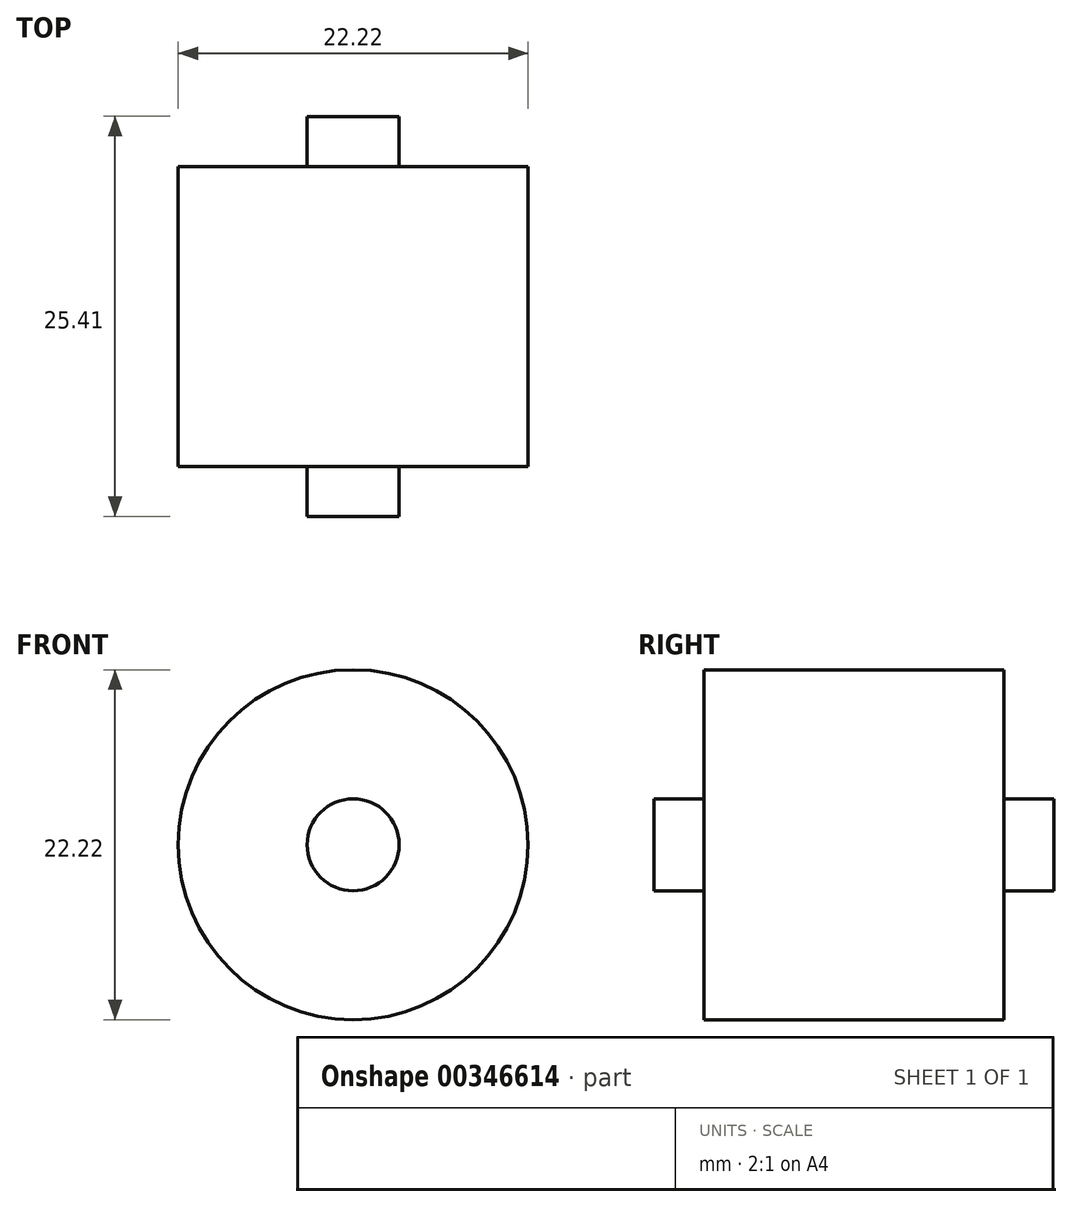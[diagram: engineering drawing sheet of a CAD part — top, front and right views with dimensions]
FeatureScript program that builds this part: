
annotation { "Feature Type Name" : "Feature", "Feature Type Description" : "" }
export const myFeature = defineFeature(function(context is Context, id is Id, definition is map)
    precondition{}
    {
        {
            var Q0;
            Q0=qCreatedBy(makeId("Front.planeOp"),FACE);
            var sketch = newSketch(context, id + "F0", { "sketchPlane" : qUnion([Q0])});
            skCircle(sketch, "E0", {"center": v(0, 0) * mm, "radius": 11.11 * mm});
            skSolve(sketch);
        }
        {
            var Q0;
            Q0 = qSketchRegion(id + "F0", true);
            extrude(context, id + "F1", {"entities" : qUnion([Q0]), "depth" : 19.05 * mm});
        }
        {
            var Q0;
            Q0=makeQuery(id+"F1.opExtrude","CAP_FACE",FACE,{"disambiguationData":[OSD([sQuery(id+"F0.wireOp",EDGE,"E0")])],"isStart":false});
            var sketch = newSketch(context, id + "F2", { "sketchPlane" : qUnion([Q0])});
            skCircle(sketch, "E1.0", {"center": v(0, 0) * mm, "radius": 11.11 * mm});
            skCircle(sketch, "E2", {"center": v(0, 0) * mm, "radius": 2.92 * mm});
            skSolve(sketch);
        }
        {
            var Q0;
            Q0=makeQuery(id+"F2.imprint","IMPRINT",FACE,{"disambiguationData":[TD([[makeQuery(id+"F2.imprint","IMPRINT",EDGE,{"derivedFrom":sQuery(id+"F2.wireOp",EDGE,"E2")}),1.0]])]});
            var Q1;
            Q1=sQuery(id+"F2.wireOp",EDGE,"E2");
            extrude(context, id + "F3", {"entities" : qUnion([Q0]), "operationType" : NewBodyOperationType.ADD, "surfaceEntities" : qUnion([Q1]), "depth" : 3.17 * mm});
        }
        {
            var Q0;
            Q0=makeQuery(id+"F1.opExtrude","CAP_FACE",FACE,{"disambiguationData":[OSD([sQuery(id+"F0.wireOp",EDGE,"E0")])],"isStart":true});
            var sketch = newSketch(context, id + "F4", { "sketchPlane" : qUnion([Q0])});
            skCircle(sketch, "E3", {"center": v(0, 0) * mm, "radius": 2.92 * mm});
            skSolve(sketch);
        }
        {
            var Q0;
            Q0=makeQuery(id+"F4.imprint","IMPRINT",FACE,{"disambiguationData":[TD([[makeQuery(id+"F4.imprint","IMPRINT",EDGE,{"derivedFrom":sQuery(id+"F4.wireOp",EDGE,"E3")}),1.0]])]});
            extrude(context, id + "F5", {"entities" : qUnion([Q0]), "operationType" : NewBodyOperationType.ADD, "depth" : 3.17 * mm});
        }
    });
